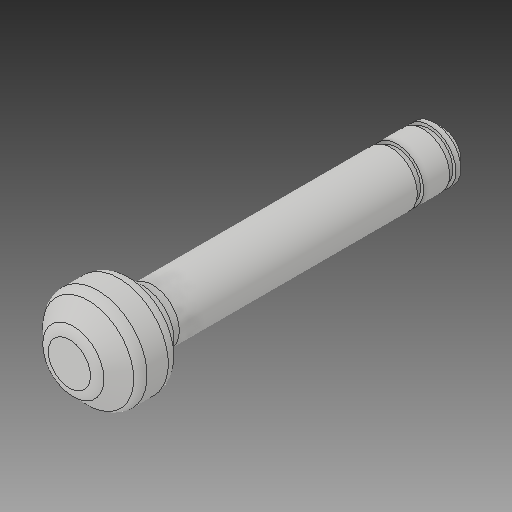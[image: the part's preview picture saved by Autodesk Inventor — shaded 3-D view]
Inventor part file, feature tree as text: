
AUTODESK INVENTOR PART (.ipt)
format: ipt  version: 2017 (Build 210142000, 142)  size: 128,512 bytes
history: native  units: in
note: dims shown in document units (in); Inventor stores cm internally (conversion verified against a paired STEP export)
features: chamfer x1
ambient origin geometry x8: Origin, YZ Plane, XZ Plane, XY Plane, X Axis, Y Axis, Z Axis, Center Point
bodies: Solid1 (feature_tree)
feature tree (1):
  chamfer  "Chamfer1"  [1 undecoded]
note: 1 required parameter value undecoded (feature->parameter linkage not recoverable at this tier; creation-order binding heuristic only, values carry confidence <= 0.55)
